# Revit family: 702-50-103-DN50-600
name_source: partatom
category: Pipe Accessories
units: mm (PartAtom-declared; Revit-internal decimal feet)

## family parameters
Always vertical = Yes
Cut with Voids When Loaded = No
Part Type = Valve - Breaks Into
Round Connector Dimension = Use Diameter
Shared = No
Work Plane-Based = No

## types (14) — shared parameters
DN050 = Yes
DN050_PN10/16 = 702-050-50-134
DN065 = Yes
DN065_PN10/16 = 702-065-50-134
DN080 = Yes
DN080_PN10/16 = 702-080-50-134
DN100 = Yes
DN100_PN10/16 = 702-100-50-134
DN125 = Yes
DN125_PN10/16 = 702-125-50-134
DN150 = Yes
DN150_PN10/16 = 702-150-50-134
DN200 = Yes
DN200_PN10 = 702-200-50-034
DN250_PN10 = 702-250-50-034
DN300 = Yes
DN300_PN10 = 702-300-50-034
DN350 = Yes
DN350_PN10 = 702-350-50-034
DN400 = Yes
DN400_PN10 = 702-400-50-034
DN450 = Yes
DN450_PN10 = 702-450-50-034
DN500 = Yes
DN500_PN10 = 702-500-50-034
DN600 = Yes
DN600_PN10 = 702-600-50-034
Description_ = AVK KNIFE GATE VALVE
Search_table = 702-50-103-DN50-600
URL product pages = https://www.avkvalves.com

## per-type parameters (varying)
| type | B2_Ref | Body_width | Bonnet_height | Bonnet_height_2 | Flange_Thickness | H3 | H_Ref | Hc | Ho | ID | L | L2 | Name_Ref | Neck_Rod | Nominal Diameter (DN) | W | W2 | W3 |
| DN 050 | 78 mm  [stored 0.255906 ft] | 87 mm | 273 mm | 150 mm | 5 mm  [stored 0.0164042 ft] | 472 mm | 113 mm | 300 mm | 407 mm | 25 mm  [stored 0.082021 ft] | 43 mm  [stored 0.141076 ft] | 47 mm | 169 mm | 10 mm  [stored 0.0328084 ft] | 50 mm  [stored 0.164042 ft] | 130 mm | 65 mm  [stored 0.213255 ft] | 54 mm |
| DN 065 | 86 mm | 95 mm  [stored 0.31168 ft] | 295 mm | 163 mm | 5 mm  [stored 0.0164042 ft] | 516 mm | 124 mm | 325 mm | 444 mm | 33 mm | 46 mm  [stored 0.150919 ft] | 51 mm | 186 mm | 10 mm  [stored 0.0328084 ft] | 65 mm  [stored 0.213255 ft] | 143 mm | 72 mm | 60 mm  [stored 0.19685 ft] |
| DN 080 | 110 mm | 122 mm | 325 mm | 179 mm | 5 mm  [stored 0.0164042 ft] | 591 mm | 159 mm | 357 mm | 499 mm | 40 mm  [stored 0.131234 ft] | 46 mm  [stored 0.150919 ft] | 51 mm | 238 mm | 10 mm  [stored 0.0328084 ft] | 80 mm  [stored 0.262467 ft] | 183 mm | 92 mm | 76 mm |
| DN 100 | 121 mm | 135 mm | 356 mm | 196 mm | 5 mm  [stored 0.0164042 ft] | 684 mm | 175 mm | 392 mm | 582 mm | 50 mm  [stored 0.164042 ft] | 52 mm | 57 mm | 263 mm | 10 mm  [stored 0.0328084 ft] | 100 mm  [stored 0.328084 ft] | 202 mm | 101 mm  [stored 0.331365 ft] | 84 mm |
| DN 125 | 137 mm | 153 mm | 389 mm | 214 mm | 5 mm  [stored 0.0164042 ft] | 733 mm | 198 mm | 428 mm | 618 mm | 63 mm | 56 mm  [stored 0.183727 ft] | 62 mm | 298 mm | 10 mm  [stored 0.0328084 ft] | 125 mm | 229 mm | 115 mm | 95 mm  [stored 0.31168 ft] |
| DN 150 | 160 mm | 178 mm | 464 mm | 255 mm | 5 mm  [stored 0.0164042 ft] | 867 mm | 231 mm | 510 mm | 732 mm | 75 mm  [stored 0.246063 ft] | 56 mm  [stored 0.183727 ft] | 62 mm | 347 mm | 10 mm  [stored 0.0328084 ft] | 150 mm | 267 mm | 134 mm | 111 mm |
| DN 200 | 196 mm | 217 mm | 555 mm | 305 mm | 10 mm  [stored 0.0328084 ft] | 1045 mm | 283 mm | 610 mm | 882 mm | 100 mm  [stored 0.328084 ft] | 60 mm  [stored 0.19685 ft] | 66 mm  [stored 0.216535 ft] | 424 mm | 20 mm  [stored 0.0656168 ft] | 200 mm | 326 mm | 163 mm | 136 mm |
| DN 300 | 271 mm | 301 mm | 758 mm | 417 mm | 15 mm  [stored 0.0492126 ft] | 1445 mm | 391 mm | 834 mm | 1219 mm | 150 mm | 78 mm  [stored 0.255906 ft] | 86 mm | 586 mm | 30 mm  [stored 0.0984252 ft] | 300 mm | 451 mm | 226 mm | 188 mm |
| DN 350 | 311 mm | 345 mm | 843 mm | 464 mm | 15 mm  [stored 0.0492126 ft] | 1621 mm | 449 mm | 927 mm | 1362 mm | 175 mm | 78 mm  [stored 0.255906 ft] | 86 mm | 673 mm | 30 mm  [stored 0.0984252 ft] | 350 mm | 518 mm | 259 mm | 216 mm |
| DN 400 | 346 mm | 384 mm | 941 mm | 518 mm | 20 mm  [stored 0.0656168 ft] | 1800 mm | 499 mm | 1035 mm | 1510 mm | 200 mm | 90 mm  [stored 0.295276 ft] | 99 mm  [stored 0.324803 ft] | 749 mm | 40 mm  [stored 0.131234 ft] | 400 mm | 576 mm | 288 mm | 240 mm |
| DN 450 | 371 mm | 412 mm | 1061 mm | 584 mm | 20 mm  [stored 0.0656168 ft] | 2030 mm | 536 mm | 1167 mm | 1717 mm | 225 mm | 90 mm  [stored 0.295276 ft] | 99 mm  [stored 0.324803 ft] | 803 mm | 40 mm  [stored 0.131234 ft] | 450 mm | 618 mm | 309 mm | 258 mm |
| DN 500 | 419 mm | 465 mm | 1101 mm | 606 mm | 20 mm  [stored 0.0656168 ft] | 2175 mm | 605 mm | 1211 mm | 1826 mm | 250 mm | 95 mm  [stored 0.31168 ft] | 105 mm  [stored 0.344488 ft] | 907 mm | 40 mm  [stored 0.131234 ft] | 500 mm | 698 mm | 349 mm | 291 mm |
| DN 600 | 490 mm | 545 mm | 1273 mm | 700 mm | 20 mm  [stored 0.0656168 ft] | 2527 mm | 708 mm | 1400 mm | 2115 mm | 300 mm | 105 mm  [stored 0.344488 ft] | 116 mm | 1062 mm | 40 mm  [stored 0.131234 ft] | 600 mm | 817 mm | 409 mm | 340 mm |
| DN 250 | 237 mm | 263 mm | 651 mm | 358 mm | 10 mm  [stored 0.0328084 ft] | 1243 mm | 342 mm | 716 mm | 1044 mm | 125 mm | 68 mm  [stored 0.223097 ft] | 75 mm  [stored 0.246063 ft] | 514 mm | 20 mm  [stored 0.0656168 ft] | 250 mm | 395 mm | 198 mm | 165 mm |

note: [stored X ft] marks values corroborated as IEEE doubles in the binary element streams (Revit-internal decimal feet)

## geometry (parser evidence)
native form markers: Sweep x6
no freeform markers — native parametric forms only
